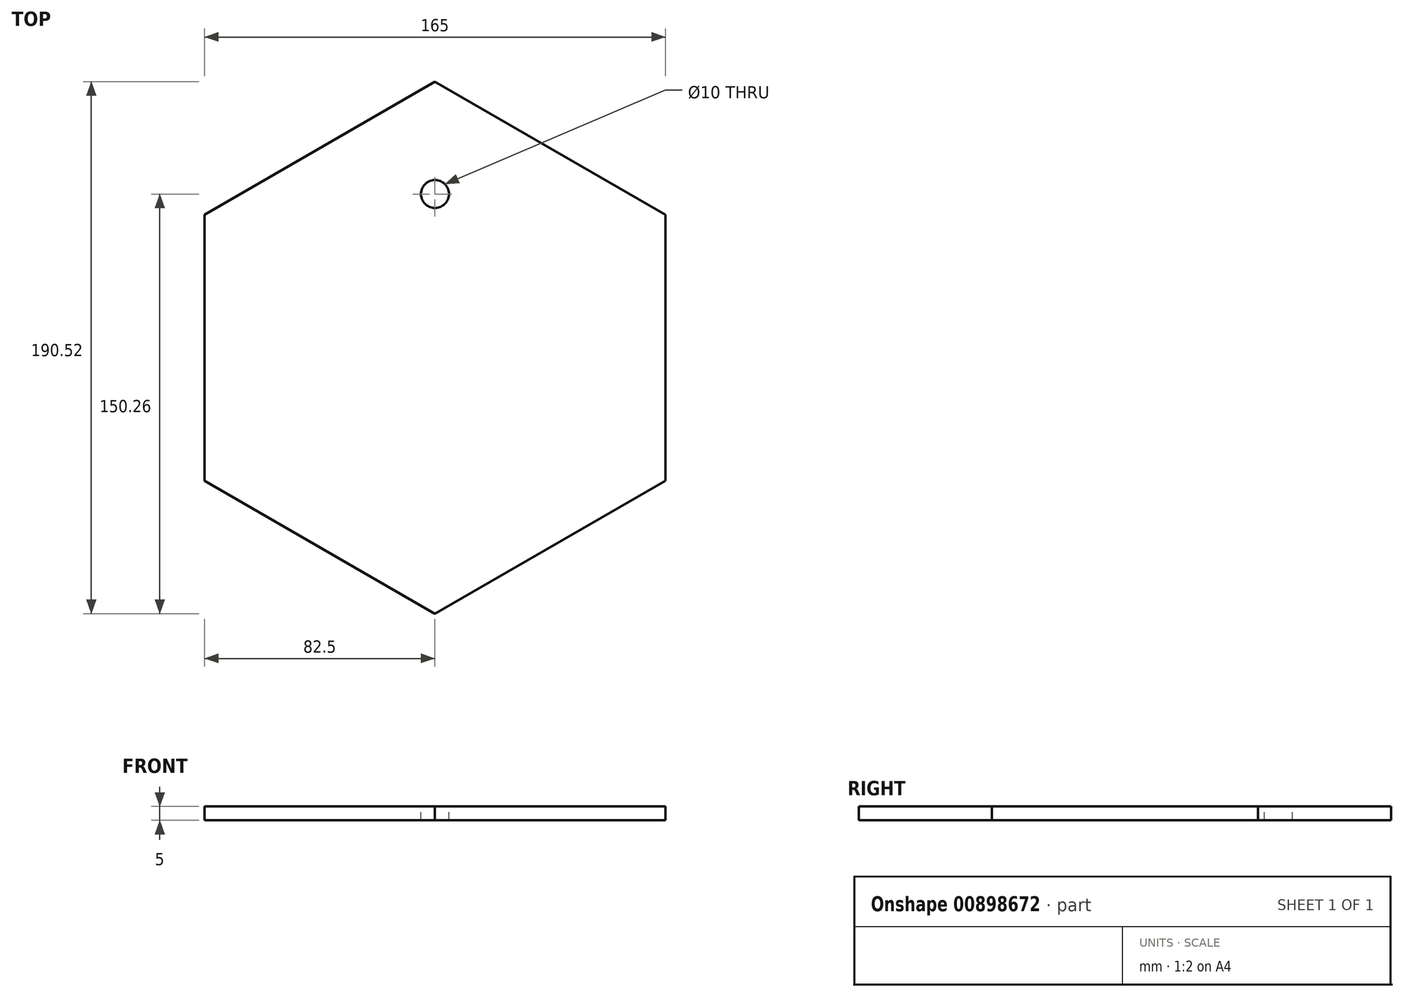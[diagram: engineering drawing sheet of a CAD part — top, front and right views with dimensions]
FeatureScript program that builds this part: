
annotation { "Feature Type Name" : "Feature", "Feature Type Description" : "" }
export const myFeature = defineFeature(function(context is Context, id is Id, definition is map)
    precondition{}
    {
        {
            var Q0;
            Q0=qCreatedBy(makeId("Top.planeOp"),FACE);
            var sketch = newSketch(context, id + "F0", { "sketchPlane" : qUnion([Q0])});
            skCircle(sketch, "E0", {"center": v(0, 0) * mm, "radius": 80 * mm, "construction": true});
            skCircle(sketch, "E1", {"center": v(0, 0) * mm, "radius": 75 * mm, "construction": true});
            skCircle(sketch, "E2.cCircle", {"center": v(0, 0) * mm, "radius": 82.5 * mm, "construction": true});
            skLineSegment(sketch, "E2.0", {"start": v(-82.5, -47.63) * mm, "end": v(-82.5, 47.63) * mm});
            skLineSegment(sketch, "E2.1", {"start": v(-82.5, 47.63) * mm, "end": v(0, 95.26) * mm});
            skLineSegment(sketch, "E2.2", {"start": v(0, 95.26) * mm, "end": v(82.5, 47.63) * mm});
            skLineSegment(sketch, "E2.3", {"start": v(82.5, 47.63) * mm, "end": v(82.5, -47.63) * mm});
            skLineSegment(sketch, "E2.4", {"start": v(82.5, -47.63) * mm, "end": v(0, -95.26) * mm});
            skLineSegment(sketch, "E2.5", {"start": v(0, -95.26) * mm, "end": v(-82.5, -47.63) * mm});
            skPoint(sketch, "E2.0.midPoint", {"position": v(-82.5, 0) * mm});
            skSolve(sketch);
        }
        {
            var Q0;
            Q0=qCreatedBy(makeId("Top.planeOp"),FACE);
            var sketch = newSketch(context, id + "F1", { "sketchPlane" : qUnion([Q0])});
            skCircle(sketch, "E3.cCircle", {"center": v(0, 0) * mm, "radius": 82.5 * mm, "construction": true});
            skLineSegment(sketch, "E3.0", {"start": v(-82.5, -47.63) * mm, "end": v(-82.5, 47.63) * mm});
            skLineSegment(sketch, "E3.1", {"start": v(-82.5, 47.63) * mm, "end": v(0, 95.26) * mm});
            skLineSegment(sketch, "E3.2", {"start": v(0, 95.26) * mm, "end": v(82.5, 47.63) * mm});
            skLineSegment(sketch, "E3.3", {"start": v(82.5, 47.63) * mm, "end": v(82.5, -47.63) * mm});
            skLineSegment(sketch, "E3.4", {"start": v(82.5, -47.63) * mm, "end": v(0, -95.26) * mm});
            skLineSegment(sketch, "E3.5", {"start": v(0, -95.26) * mm, "end": v(-82.5, -47.63) * mm});
            skPoint(sketch, "E3.0.midPoint", {"position": v(-82.5, 0) * mm});
            skSolve(sketch);
        }
        {
            var Q0;
            Q0 = qSketchRegion(id + "F1", true);
            extrude(context, id + "F2", {"entities" : qUnion([Q0]), "depth" : 5 * mm, "offsetDistance" : 25 * mm});
        }
        {
            var Q0;
            Q0=makeQuery(id+"F2.opExtrude","CAP_FACE",FACE,{"disambiguationData":[OSD([sQuery(id+"F1.wireOp",EDGE,"E3.0"),sQuery(id+"F1.wireOp",EDGE,"E3.1"),sQuery(id+"F1.wireOp",EDGE,"E3.2"),sQuery(id+"F1.wireOp",EDGE,"E3.3"),sQuery(id+"F1.wireOp",EDGE,"E3.4"),sQuery(id+"F1.wireOp",EDGE,"E3.5")])],"isStart":false});
            var sketch = newSketch(context, id + "F3", { "sketchPlane" : qUnion([Q0])});
            skCircle(sketch, "E4", {"center": v(0, 55) * mm, "radius": 5 * mm});
            skSolve(sketch);
        }
        {
            var Q0;
            Q0 = qSketchRegion(id + "F3", true);
            extrude(context, id + "F4", {"entities" : qUnion([Q0]), "operationType" : NewBodyOperationType.REMOVE, "oppositeDirection" : true, "depth" : 25 * mm, "offsetDistance" : 25 * mm});
        }
    });
